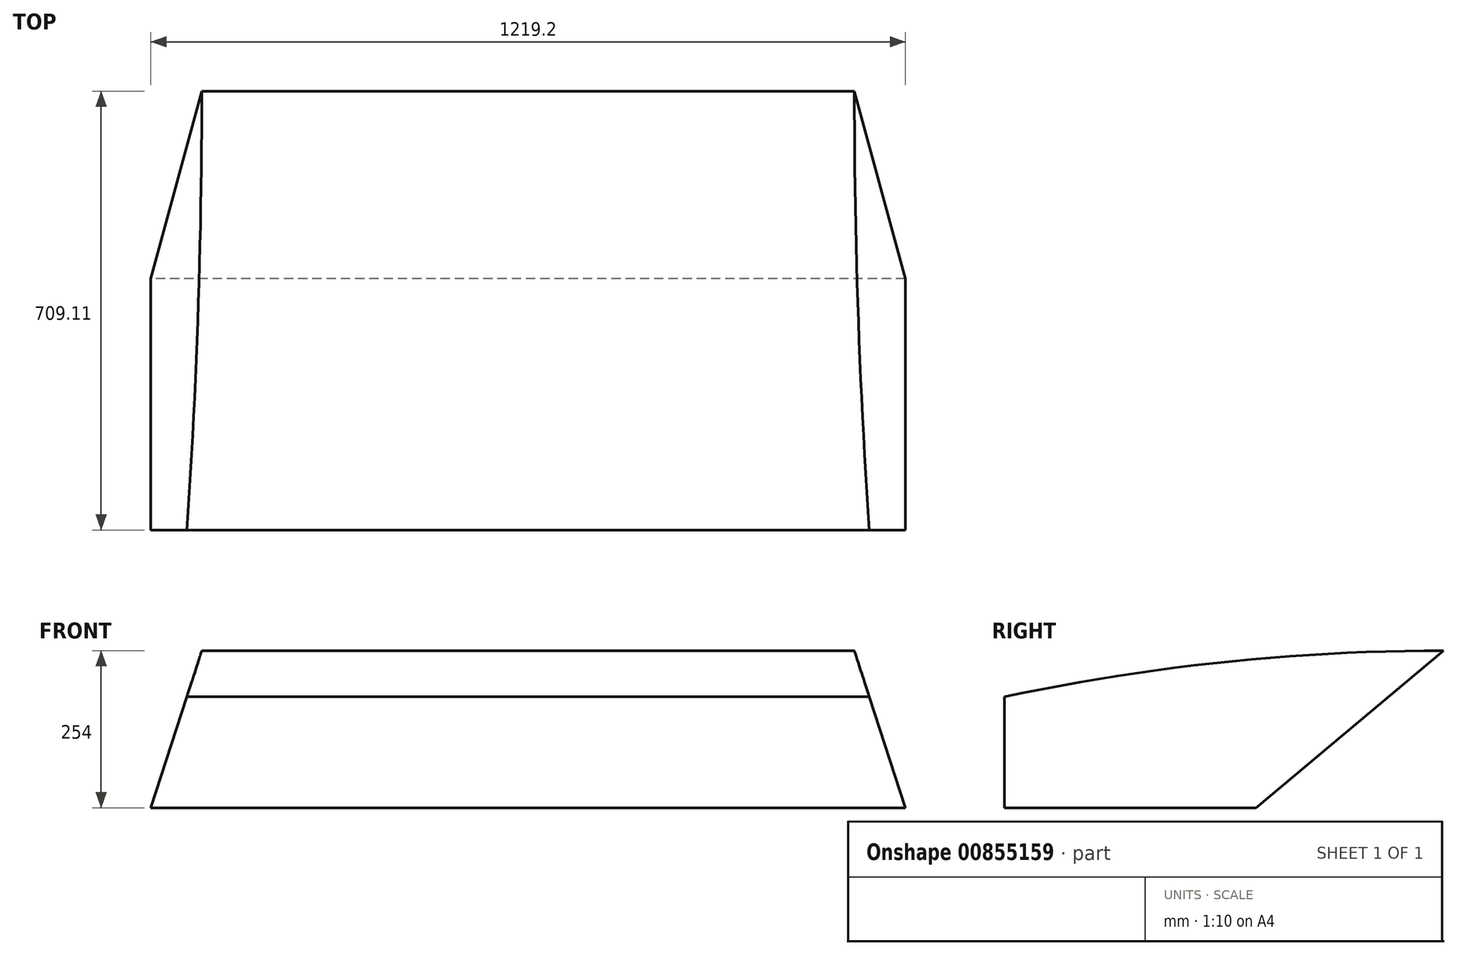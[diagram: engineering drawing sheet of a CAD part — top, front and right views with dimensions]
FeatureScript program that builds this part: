
annotation { "Feature Type Name" : "Feature", "Feature Type Description" : "" }
export const myFeature = defineFeature(function(context is Context, id is Id, definition is map)
    precondition{}
    {
        {
            var Q0;
            Q0=qCreatedBy(makeId("Right.planeOp"),FACE);
            var sketch = newSketch(context, id + "F0", { "sketchPlane" : qUnion([Q0])});
            skLineSegment(sketch, "E0", {"start": v(-406.4, 0) * mm, "end": v(0, 0) * mm});
            skLineSegment(sketch, "E1", {"start": v(0, 0) * mm, "end": v(302.7, 254) * mm});
            skLineSegment(sketch, "E2", {"start": v(-406.4, 179.47) * mm, "end": v(-406.4, 0) * mm});
            skArc(sketch, "E3", {"start": v(302.7, 254) * mm, "mid": v(-53.8, 235.32) * mm, "end": v(-406.4, 179.47) * mm});
            skLineSegment(sketch, "E4", {"start": v(514.43, 254) * mm, "end": v(-139.6, 254) * mm, "construction": true});
            skLineSegment(sketch, "E5", {"start": v(-625.43, 132.91) * mm, "end": v(99.24, 286.95) * mm, "construction": true});
            skSolve(sketch);
        }
        {
            var Q0;
            Q0=makeQuery(id+"F0.imprint","IMPRINT",FACE,{"disambiguationData":[TD([[makeQuery(id+"F0.imprint","IMPRINT",EDGE,{"derivedFrom":sQuery(id+"F0.wireOp",EDGE,"E0")}),1.0]])]});
            extrude(context, id + "F1", {"entities" : qUnion([Q0]), "depth" : 609.6 * mm, "offsetDistance" : 25.4 * mm});
        }
        {
            var Q0;
            Q0=makeQuery(id+"F1.opExtrude","SWEPT_FACE",FACE,{"disambiguationData":[OSD([sQuery(id+"F0.wireOp",EDGE,"E2")])]});
            var sketch = newSketch(context, id + "F2", { "sketchPlane" : qUnion([Q0])});
            skLineSegment(sketch, "E6", {"start": v(609.6, 0) * mm, "end": v(519.08, 278.6) * mm});
            skLineSegment(sketch, "E7", {"start": v(519.08, 278.6) * mm, "end": v(609.6, 278.6) * mm});
            skLineSegment(sketch, "E8", {"start": v(609.6, 278.6) * mm, "end": v(609.6, 0) * mm});
            skSolve(sketch);
        }
        {
            var Q0;
            {var subQ1=sQuery(id+"F2.wireOp",EDGE,"E6");var subQ2=sQuery(id+"F0.wireOp",EDGE,"E2");var subQ4=makeQuery(id+"F1.opExtrude","SWEPT_EDGE",EDGE,{"disambiguationData":[OSD([subQ2,sQuery(id+"F0.wireOp",EDGE,"E3")])]});var subQ5=makeQuery(id+"F2.imprint","INTERSECT",VERTEX,{"derivedFrom":[subQ4,subQ1]});Q0=makeQuery(id+"F2.imprint","IMPRINT",FACE,{"disambiguationData":[TD([[makeQuery(id+"F2.imprint","IMPRINT",EDGE,{"disambiguationData":[TD([[subQ5,1.0]])],"derivedFrom":subQ1}),-1.0]])]});}
            var Q1;
            {var subQ0=sQuery(id+"F2.wireOp",EDGE,"E7");Q1=makeQuery(id+"F2.imprint","IMPRINT",FACE,{"disambiguationData":[TD([[makeQuery(id+"F2.imprint","IMPRINT",EDGE,{"derivedFrom":subQ0}),-1.0]])]});}
            extrude(context, id + "F3", {"entities" : qUnion([Q0, Q1]), "operationType" : NewBodyOperationType.REMOVE, "endBound" : BoundingType.THROUGH_ALL, "oppositeDirection" : true, "depth" : 25.4 * mm, "offsetDistance" : 25.4 * mm});
        }
        {
            var Q0;
            Q0=makeQuery(id+"F1.opExtrude","SWEPT_BODY",BODY,{"disambiguationData":[OSD([sQuery(id+"F0.wireOp",EDGE,"E0"),sQuery(id+"F0.wireOp",EDGE,"E1"),sQuery(id+"F0.wireOp",EDGE,"E2"),sQuery(id+"F0.wireOp",EDGE,"E3")])]});
            var Q1;
            Q1=qCreatedBy(makeId("Right.planeOp"),FACE);
            mirror(context, id + "F4", {"operationType" : NewBodyOperationType.ADD, "entities" : qUnion([Q0]), "mirrorPlane" : qUnion([Q1])});
        }
    });
